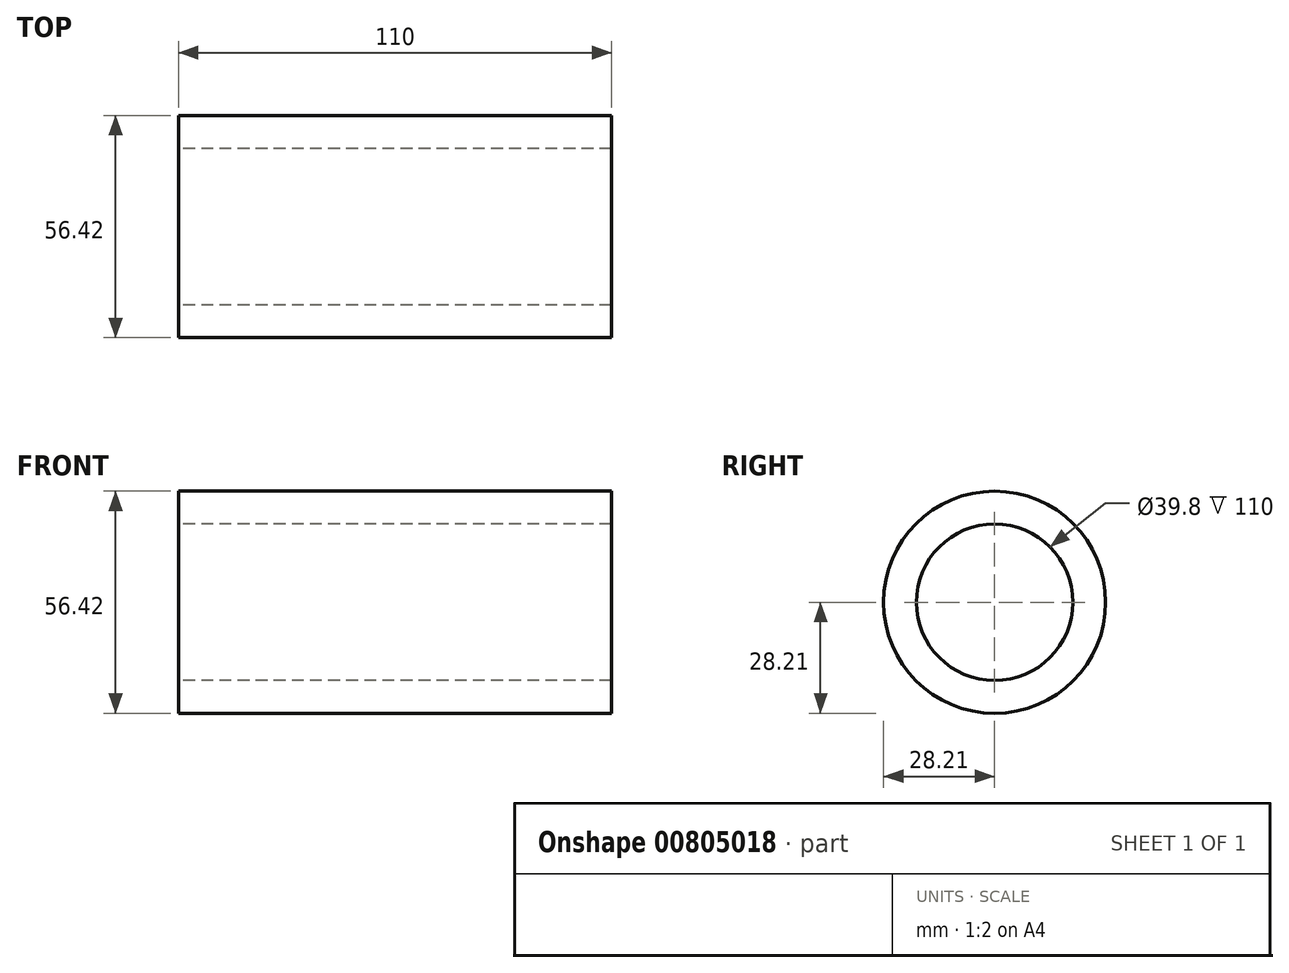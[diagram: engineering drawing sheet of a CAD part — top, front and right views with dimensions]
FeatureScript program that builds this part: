
annotation { "Feature Type Name" : "Feature", "Feature Type Description" : "" }
export const myFeature = defineFeature(function(context is Context, id is Id, definition is map)
    precondition{}
    {
        {
            var Q0;
            Q0=qCreatedBy(makeId("Right.planeOp"),FACE);
            var sketch = newSketch(context, id + "F0", { "sketchPlane" : qUnion([Q0])});
            skCircle(sketch, "E0", {"center": v(0, 0) * mm, "radius": 28.2 * mm});
            skCircle(sketch, "E1", {"center": v(0, 0) * mm, "radius": 19.9 * mm});
            skSolve(sketch);
        }
        {
            var Q0;
            Q0=makeQuery(id+"F0.imprint","IMPRINT",FACE,{"disambiguationData":[TD([[makeQuery(id+"F0.imprint","IMPRINT",EDGE,{"derivedFrom":sQuery(id+"F0.wireOp",EDGE,"E0")}),1.0]])]});
            extrude(context, id + "F1", {"entities" : qUnion([Q0]), "endBound" : BoundingType.SYMMETRIC, "depth" : 110 * mm, "offsetDistance" : 25.4 * mm});
        }
    });
